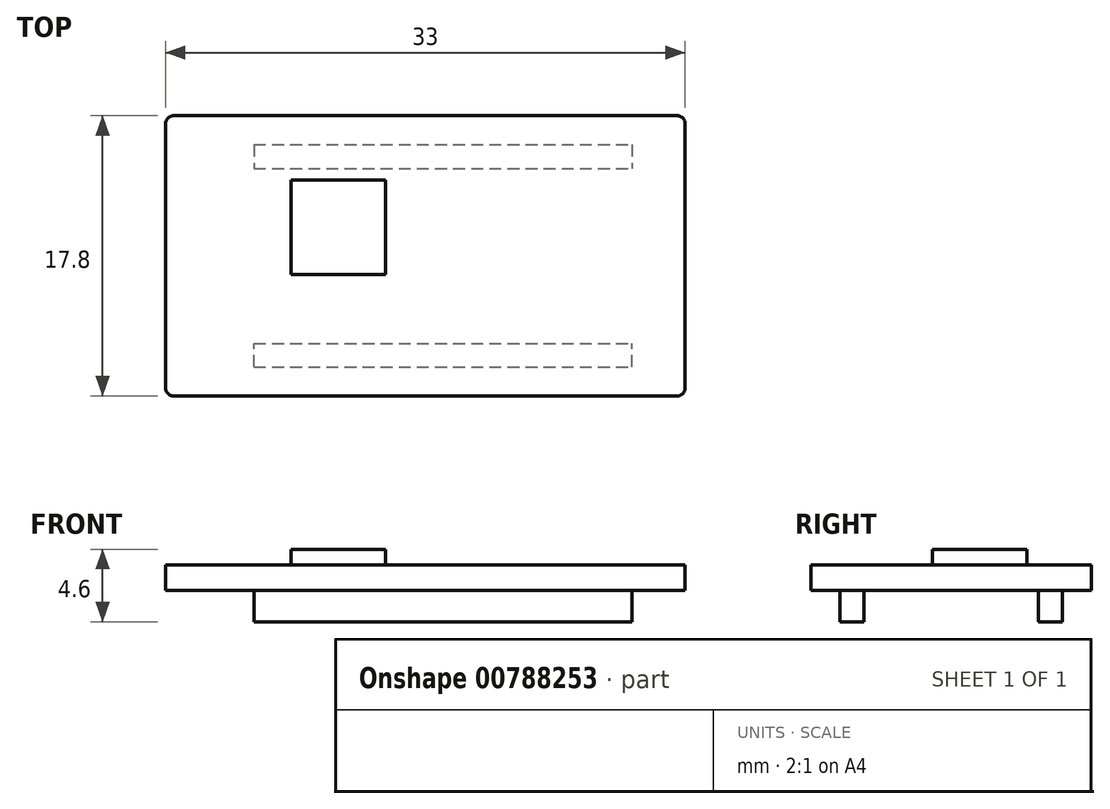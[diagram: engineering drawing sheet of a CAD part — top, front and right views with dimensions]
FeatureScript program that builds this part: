
annotation { "Feature Type Name" : "Feature", "Feature Type Description" : "" }
export const myFeature = defineFeature(function(context is Context, id is Id, definition is map)
    precondition{}
    {
        {
            var Q0;
            Q0=qCreatedBy(makeId("Top.planeOp"),FACE);
            var sketch = newSketch(context, id + "F0", { "sketchPlane" : qUnion([Q0])});
            skLineSegment(sketch, "E0.bottom", {"start": v(-13.97, 7.78) * mm, "end": v(19.03, 7.78) * mm});
            skLineSegment(sketch, "E0.top", {"start": v(-13.97, -10.02) * mm, "end": v(19.03, -10.02) * mm});
            skLineSegment(sketch, "E0.left", {"start": v(-13.97, 7.78) * mm, "end": v(-13.97, -10.02) * mm});
            skLineSegment(sketch, "E0.right", {"start": v(19.03, 7.78) * mm, "end": v(19.03, -10.02) * mm});
            skSolve(sketch);
        }
        {
            var Q0;
            Q0=makeQuery(id+"F0.imprint","IMPRINT",FACE,{"disambiguationData":[TD([[makeQuery(id+"F0.imprint","IMPRINT",EDGE,{"derivedFrom":sQuery(id+"F0.wireOp",EDGE,"E0.bottom")}),-1.0]])]});
            extrude(context, id + "F1", {"entities" : qUnion([Q0]), "depth" : 1.6 * mm, "offsetDistance" : 25 * mm});
        }
        {
            var Q0;
            Q0=makeQuery(id+"F1.opExtrude","SWEPT_EDGE",EDGE,{"disambiguationData":[OSD([sQuery(id+"F0.wireOp",EDGE,"E0.top"),sQuery(id+"F0.wireOp",EDGE,"E0.right")])]});
            var Q1;
            Q1=makeQuery(id+"F1.opExtrude","SWEPT_EDGE",EDGE,{"disambiguationData":[OSD([sQuery(id+"F0.wireOp",EDGE,"E0.top"),sQuery(id+"F0.wireOp",EDGE,"E0.left")])]});
            var Q2;
            Q2=makeQuery(id+"F1.opExtrude","SWEPT_EDGE",EDGE,{"disambiguationData":[OSD([sQuery(id+"F0.wireOp",EDGE,"E0.bottom"),sQuery(id+"F0.wireOp",EDGE,"E0.right")])]});
            var Q3;
            Q3=makeQuery(id+"F1.opExtrude","SWEPT_EDGE",EDGE,{"disambiguationData":[OSD([sQuery(id+"F0.wireOp",EDGE,"E0.bottom"),sQuery(id+"F0.wireOp",EDGE,"E0.left")])]});
            fillet(context, id + "F2", {"entities" : qUnion([Q0, Q1, Q2, Q3]), "radius" : 0.5 * mm, "tangentPropagation" : true, "allowEdgeOverflow" : false});
        }
        {
            var Q0;
            Q0=makeQuery(id+"F1.opExtrude","CAP_FACE",FACE,{"disambiguationData":[OSD([sQuery(id+"F0.wireOp",EDGE,"E0.bottom"),sQuery(id+"F0.wireOp",EDGE,"E0.top"),sQuery(id+"F0.wireOp",EDGE,"E0.left"),sQuery(id+"F0.wireOp",EDGE,"E0.right")])],"isStart":false});
            var sketch = newSketch(context, id + "F3", { "sketchPlane" : qUnion([Q0])});
            skLineSegment(sketch, "E1.bottom", {"start": v(-6, -2.32) * mm, "end": v(0, -2.32) * mm});
            skLineSegment(sketch, "E1.top", {"start": v(-6, 3.68) * mm, "end": v(0, 3.68) * mm});
            skLineSegment(sketch, "E1.left", {"start": v(-6, -2.32) * mm, "end": v(-6, 3.68) * mm});
            skLineSegment(sketch, "E1.right", {"start": v(0, -2.32) * mm, "end": v(0, 3.68) * mm});
            skSolve(sketch);
        }
        {
            var Q0;
            Q0=makeQuery(id+"F3.imprint","IMPRINT",FACE,{"disambiguationData":[TD([[makeQuery(id+"F3.imprint","IMPRINT",EDGE,{"derivedFrom":sQuery(id+"F3.wireOp",EDGE,"E1.bottom")}),1.0]])]});
            extrude(context, id + "F4", {"entities" : qUnion([Q0]), "operationType" : NewBodyOperationType.ADD, "depth" : 1 * mm, "offsetDistance" : 25 * mm});
        }
        {
            var Q0;
            Q0=makeQuery(id+"F1.opExtrude","CAP_FACE",FACE,{"disambiguationData":[OSD([sQuery(id+"F0.wireOp",EDGE,"E0.bottom"),sQuery(id+"F0.wireOp",EDGE,"E0.top"),sQuery(id+"F0.wireOp",EDGE,"E0.left"),sQuery(id+"F0.wireOp",EDGE,"E0.right")])],"isStart":true});
            var sketch = newSketch(context, id + "F5", { "sketchPlane" : qUnion([Q0])});
            skLineSegment(sketch, "E2.bottom", {"start": v(-8.35, 8.18) * mm, "end": v(15.65, 8.18) * mm});
            skLineSegment(sketch, "E2.top", {"start": v(-8.35, 6.68) * mm, "end": v(15.65, 6.68) * mm});
            skLineSegment(sketch, "E2.left", {"start": v(-8.35, 8.18) * mm, "end": v(-8.35, 6.68) * mm});
            skLineSegment(sketch, "E2.right", {"start": v(15.65, 8.18) * mm, "end": v(15.65, 6.68) * mm});
            skLineSegment(sketch, "E3", {"start": v(-13.97, 1.12) * mm, "end": v(19.03, 1.12) * mm, "construction": true});
            skLineSegment(sketch, "E4.MirrorCS", {"start": v(-8.35, -4.43) * mm, "end": v(15.65, -4.43) * mm});
            skLineSegment(sketch, "E5.MirrorCS", {"start": v(-8.35, -5.93) * mm, "end": v(15.65, -5.93) * mm});
            skLineSegment(sketch, "E6.MirrorCS", {"start": v(15.65, -5.93) * mm, "end": v(15.65, -4.43) * mm});
            skLineSegment(sketch, "E7.MirrorCS", {"start": v(-8.35, -5.93) * mm, "end": v(-8.35, -4.43) * mm});
            skSolve(sketch);
        }
        {
            var Q0;
            Q0=makeQuery(id+"F5.imprint","IMPRINT",FACE,{"disambiguationData":[TD([[makeQuery(id+"F5.imprint","IMPRINT",EDGE,{"derivedFrom":sQuery(id+"F5.wireOp",EDGE,"E2.bottom")}),-1.0]])]});
            var Q1;
            Q1=makeQuery(id+"F5.imprint","IMPRINT",FACE,{"disambiguationData":[TD([[makeQuery(id+"F5.imprint","IMPRINT",EDGE,{"derivedFrom":sQuery(id+"F5.wireOp",EDGE,"E4.MirrorCS")}),-1.0]])]});
            extrude(context, id + "F6", {"entities" : qUnion([Q0, Q1]), "operationType" : NewBodyOperationType.ADD, "depth" : 2 * mm, "offsetDistance" : 25 * mm});
        }
    });
